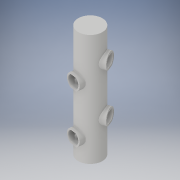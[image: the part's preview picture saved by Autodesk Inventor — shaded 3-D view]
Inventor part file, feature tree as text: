
AUTODESK INVENTOR PART (.ipt)
format: ipt  version: 2017 (Build 210142000, 142)  size: 1,877,504 bytes
history: native  units: in
note: dims shown in document units (in); Inventor stores cm internally (conversion verified against a paired STEP export)
features: extrude x32, sketch x26, other x17, loft x6, shell x1, plane x1
ambient origin geometry x8: Origin, YZ Plane, XZ Plane, XY Plane, X Axis, Y Axis, Z Axis, Center Point
bodies: Solid4 (feature_tree), Solid5 (feature_tree), Solid6 (feature_tree), Solid7 (feature_tree), Solid8 (feature_tree), Solid9 (feature_tree), Solid10 (feature_tree)
feature tree (83):
  shell  "shell and ramp"  Thickness=15.0in
  extrude  "outer cassing"  Depth=72.0in TaperAngle=0.0deg
  extrude  "bottom"  Depth=3.5in
  sketch  "Sketch2"  dims[d40=1.0in d41=0.0in d44=3.5in]
  other  "Work Axis1"
  other  "ramp"
  other  "ramp light"
  other  "top floor fill workplane"
  extrude  "top floor fill"  Depth=0.5in
  sketch  "Sketch5"  dims[d55=3.0in]
  other  "railing complete"
  other  "light ramp to complete"
  extrude  "top cap"  Depth=9.0in
  plane  "workplane sketch"
  other  "connection plane 1"
  other  "connection plane 2"
  other  "connection workplane 3"
  sketch  "Sketch19"  dims[d64=8.0in d65=1.0in d66=3.1201in d67=0.0in d68=90.0deg d69=90.0deg d70=0.0in d71=0.0in d146=9.0in]
  extrude  "bottom connection"  TaperAngle=90.0deg  [1 undecoded]
  extrude  "bottom connect to case"  TaperAngle=90.0deg  [1 undecoded]
  extrude  "connection cut"  Depth=1.0in TaperAngle=0.0deg
  extrude  "light bottom"  Depth=2.6875in TaperAngle=0.0deg
  sketch  "Sketch20"  dims[d147=1.1811in d149=360.0deg d151=90.0deg]
  extrude  "connetion 2"  Depth=1.0in TaperAngle=0.0deg
  extrude  "connection to case 2"  Depth=1.0in TaperAngle=0.0deg
  extrude  "connection cut 2"  Depth=20.15in
  extrude  "light 2"  Depth=1.0in TaperAngle=0.0deg
  loft  "connection ramp 2"
  sketch  "Sketch22"  dims[d152=90.0deg d153=90.0deg]
  extrude  "connection 3"  Depth=1.0in TaperAngle=0.0deg
  extrude  "connection to case 3"  Depth=52.15in
  extrude  "connection cut 3"  Depth=1.0in TaperAngle=0.0deg
  extrude  "light 3"  Depth=6.6667in
  loft  "connetion ramp 3"
  sketch  "Sketch23"  dims[d154=6.6667in d155=4.0in d156=1.0in d157=4.8944in d158=1.0in d159=0.0in]
  extrude  "connection 4"  TaperAngle=0.0deg  [1 undecoded]
  extrude  "connection to case 4"  Depth=1.0in TaperAngle=0.0deg
  extrude  "connection cut 4"  Depth=0.5833in
  extrude  "light 4"  TaperAngle=90.0deg  [1 undecoded]
  loft  "connection ramp 4"
  sketch  "Sketch24"  dims[d160=1.0in d161=0.0in d162=2.6875in d163=0.0in]
  extrude  "connection 5"  TaperAngle=0.0deg  [1 undecoded]
  extrude  "connection to case 5"  TaperAngle=0.0deg  [1 undecoded]
  extrude  "connection cut 5"  Depth=1.0in
  extrude  "light 5"  Depth=1.0in
  loft  "connection ramp 5"
  sketch  "Sketch25"  dims[d164=9.48in]
  extrude  "connection 6"  TaperAngle=0.0deg  [1 undecoded]
  extrude  "connection to case 6"  Depth=1.0in
  extrude  "connection cut 6"  TaperAngle=0.0deg  [1 undecoded]
  extrude  "light 6"  TaperAngle=0.0deg  [1 undecoded]
  loft  "connection ramp 6"
  sketch  "Sketch26"  dims[d165=6.6667in d166=4.0in d167=1.0in d168=4.8944in d169=1.0in d170=0.0in d171=1.0in d172=0.0in]
  extrude  "connection 7"  TaperAngle=0.0deg  [1 undecoded]
  extrude  "connection to case 7"  TaperAngle=0.0deg  [1 undecoded]
  extrude  "connection cut 7"  Depth=1.0in
  extrude  "light 7"  TaperAngle=0.0deg  [1 undecoded]
  loft  "connection ramp 7"
  sketch  "Sketch1"  dims[d1=16.0in d2=72.0in d3=0.0in]
  sketch  "Sketch4"  dims[d53=3.0in d54=0.5in]
  sketch  "Sketch27"  dims[d173=2.625in d174=0.0in]
  sketch  "Sketch28"  dims[d178=6.6667in d179=4.0in d180=1.0in d181=4.8944in d182=1.0in d183=0.0in d184=1.0in d185=0.0in]
  other  "light railing"
  other  "light railing complete"
  sketch  "Sketch29"  dims[d186=1.0in d187=0.0in d188=20.15in]
  other  "Edges1"
  sketch  "Sketch30"  dims[d189=30.81in]
  other  "Edges2"
  sketch  "Sketch31"  dims[d190=6.6667in d191=4.0in d192=1.0in d193=4.8944in d194=1.0in d195=0.0in d196=1.0in d197=0.0in]
  other  "Edges3"
  sketch  "Sketch32"  dims[d198=1.0in d199=0.0in d200=41.48in]
  other  "Edges4"
  sketch  "Sketch33"  dims[d201=6.6667in d202=4.0in d203=1.0in d204=4.8944in d205=1.0in d206=0.0in d207=1.0in d208=0.0in]
  other  "Edges5"
  sketch  "Sketch35"  dims[d209=1.0in d210=0.0in d211=52.15in]
  other  "Edges6"
  sketch  "Sketch36"  dims[d213=6.6667in d214=4.0in d215=1.0in d216=4.8944in d217=1.0in d218=0.0in d219=1.0in d220=0.0in]
  sketch  "Sketch37"  dims[d221=1.0in d222=0.0in d228=6.6667in d229=4.0in d230=1.0in d231=4.8944in]
  sketch  "Sketch38"  dims[d232=62.8in d233=1.0in d234=0.0in]
  sketch  "Sketch39"  dims[d237=1.0in d238=0.0in d239=0.0in]
  sketch  "Sketch40"  dims[d240=1.0in d241=0.0in d242=1.0in d243=0.0in]
  sketch  "Sketch41"  dims[d244=1.0in d245=0.0in d253=0.5833in d254=0.0625in d255=0.0625in d256=0.125in]
  sketch  "Sketch42"  dims[d257=2.0in d268=0.25in d269=0.125in d270=45.0deg d271=0.0892in d272=0.0884in d273=8.0in d274=1.0in d275=3.1201in d276=0.0in d277=90.0deg d278=90.0deg d279=0.0in d280=0.0in d308=3.0in d309=0.5in d310=3.0in d311=0.5833in d312=0.0625in d313=0.0625in d315=0.25in d316=0.125in d317=45.0deg d318=0.0892in d319=0.0884in d320=0.125in d321=90.0deg d322=90.0deg d323=0.0in d324=90.0deg d325=0.0in d326=90.0deg d327=1.0in d329=1.0in d330=0.0in d331=90.0deg d332=0.0in d333=90.0deg d335=1.0in d336=0.0in d337=90.0deg d338=0.0in d339=90.0deg d340=1.0in d341=0.0in d342=90.0deg d343=0.0in d344=90.0deg d346=1.0in d347=0.0in d348=90.0deg d349=0.0in d350=90.0deg d353=1.0in d354=0.0in d355=90.0deg d356=0.0in d357=90.0deg d367=0.5833in d368=0.0625in d369=0.0625in d370=0.25in d371=0.125in d372=0.0892in d373=0.0884in d374=0.125in d375=0.5833in d376=0.0625in d377=0.0625in d378=0.125in d379=1.0in d380=0.0in d381=0.5833in d382=0.0625in d383=0.0625in d384=0.125in d385=0.25in d386=0.125in d387=45.0deg d388=0.0892in d389=0.0884in d390=1.0in d391=0.0in d392=0.5833in d393=0.0625in d394=0.0625in d395=0.125in d396=0.25in d397=0.125in d398=45.0deg d399=0.0892in d400=0.0884in d401=1.0in d402=0.0in d403=0.5833in d404=0.0625in d405=0.0625in d406=0.125in d407=0.25in d408=0.125in d409=45.0deg d410=0.0892in d411=0.0884in d412=1.0in d413=0.0in d414=0.5833in d415=0.0625in d416=0.0625in d417=0.125in d418=0.25in d419=0.125in d420=45.0deg d421=0.0892in d422=0.0884in d423=1.0in d424=0.0in d425=0.5833in d426=0.0625in d427=0.0625in d428=0.125in d429=0.25in d430=0.125in d431=45.0deg d432=0.0892in d433=0.0884in d434=1.0in d435=0.0in d436=0.25in d437=0.125in d438=45.0deg d439=0.0892in d440=0.0884in d441=0.5833in d442=0.0625in d443=0.0625in d444=0.125in d445=1.0in d446=0.0in]
note: 12 required parameter values undecoded (feature->parameter linkage not recoverable at this tier; creation-order binding heuristic only, values carry confidence <= 0.55)
